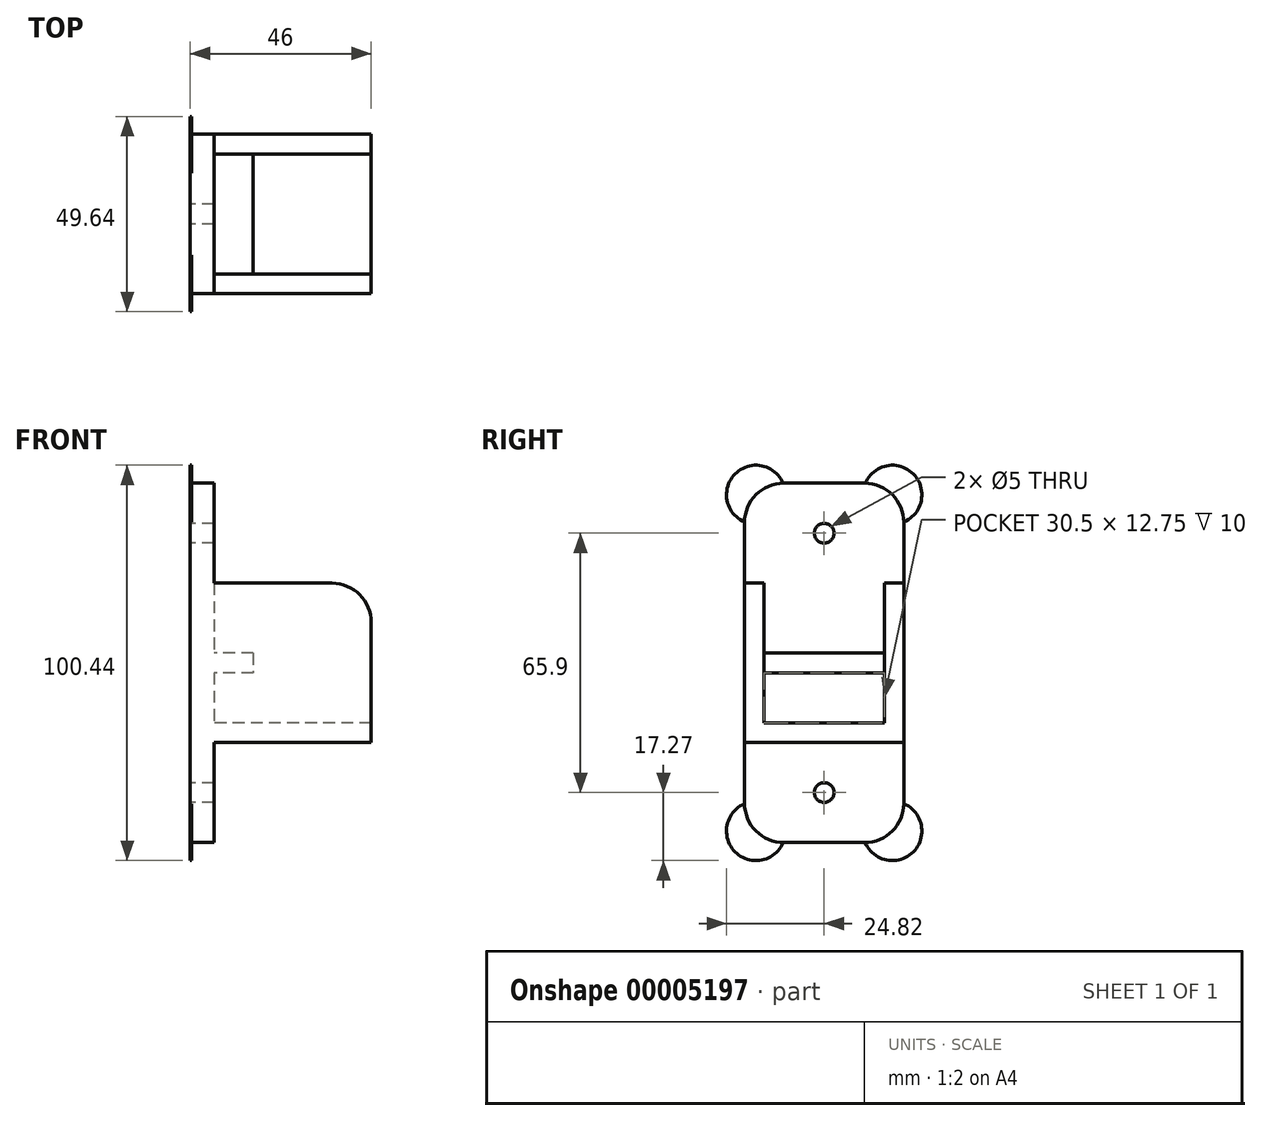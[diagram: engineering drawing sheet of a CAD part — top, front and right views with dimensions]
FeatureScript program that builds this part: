
annotation { "Feature Type Name" : "Feature", "Feature Type Description" : "" }
export const myFeature = defineFeature(function(context is Context, id is Id, definition is map)
    precondition{}
    {
        {
            var Q0;
            Q0=qCreatedBy(makeId("Right.planeOp"),FACE);
            var sketch = newSketch(context, id + "F0", { "sketchPlane" : qUnion([Q0])});
            skLineSegment(sketch, "E0.bottom", {"start": v(15.25, 15.25) * mm, "end": v(-15.25, 15.25) * mm});
            skLineSegment(sketch, "E0.top", {"start": v(15.25, -15.25) * mm, "end": v(-15.25, -15.25) * mm});
            skLineSegment(sketch, "E0.left", {"start": v(15.25, 15.25) * mm, "end": v(15.25, -15.25) * mm});
            skLineSegment(sketch, "E0.right", {"start": v(-15.25, 15.25) * mm, "end": v(-15.25, -15.25) * mm});
            skPoint(sketch, "E0.middle", {"position": v(0, 0) * mm});
            skLineSegment(sketch, "E1.bottom", {"start": v(20.25, 20.25) * mm, "end": v(-20.25, 20.25) * mm});
            skLineSegment(sketch, "E1.top", {"start": v(20.25, -20.25) * mm, "end": v(-20.25, -20.25) * mm});
            skLineSegment(sketch, "E1.left", {"start": v(20.25, 20.25) * mm, "end": v(20.25, -20.25) * mm});
            skLineSegment(sketch, "E1.right", {"start": v(-20.25, 20.25) * mm, "end": v(-20.25, -20.25) * mm});
            skSolve(sketch);
        }
        {
            var Q0;
            Q0 = qSketchRegion(id + "F0", true);
            extrude(context, id + "F1", {"entities" : qUnion([Q0]), "depth" : 40 * mm});
        }
        {
            var Q0;
            Q0=makeQuery(id+"F1.opExtrude","CAP_FACE",FACE,{"disambiguationData":[OSD([sQuery(id+"F0.wireOp",EDGE,"E0.bottom"),sQuery(id+"F0.wireOp",EDGE,"E0.top"),sQuery(id+"F0.wireOp",EDGE,"E0.left"),sQuery(id+"F0.wireOp",EDGE,"E0.right"),sQuery(id+"F0.wireOp",EDGE,"E1.bottom"),sQuery(id+"F0.wireOp",EDGE,"E1.top"),sQuery(id+"F0.wireOp",EDGE,"E1.left"),sQuery(id+"F0.wireOp",EDGE,"E1.right")])],"isStart":false});
            var sketch = newSketch(context, id + "F2", { "sketchPlane" : qUnion([Q0])});
            skLineSegment(sketch, "E2.bottom", {"start": v(15.25, 15.25) * mm, "end": v(-15.25, 15.25) * mm});
            skLineSegment(sketch, "E2.top", {"start": v(15.25, 20.25) * mm, "end": v(-15.25, 20.25) * mm});
            skLineSegment(sketch, "E2.left", {"start": v(15.25, 15.25) * mm, "end": v(15.25, 20.25) * mm});
            skLineSegment(sketch, "E2.right", {"start": v(-15.25, 15.25) * mm, "end": v(-15.25, 20.25) * mm});
            skSolve(sketch);
        }
        {
            var Q0;
            Q0 = qSketchRegion(id + "F2", true);
            extrude(context, id + "F3", {"entities" : qUnion([Q0]), "operationType" : NewBodyOperationType.REMOVE, "endBound" : BoundingType.THROUGH_ALL, "oppositeDirection" : true, "depth" : 25 * mm});
        }
        {
            var Q0;
            Q0=makeQuery(id+"F1.opExtrude","CAP_FACE",FACE,{"disambiguationData":[OSD([sQuery(id+"F0.wireOp",EDGE,"E0.bottom"),sQuery(id+"F0.wireOp",EDGE,"E0.top"),sQuery(id+"F0.wireOp",EDGE,"E0.left"),sQuery(id+"F0.wireOp",EDGE,"E0.right"),sQuery(id+"F0.wireOp",EDGE,"E1.bottom"),sQuery(id+"F0.wireOp",EDGE,"E1.top"),sQuery(id+"F0.wireOp",EDGE,"E1.left"),sQuery(id+"F0.wireOp",EDGE,"E1.right")])],"isStart":true});
            var sketch = newSketch(context, id + "F4", { "sketchPlane" : qUnion([Q0])});
            skLineSegment(sketch, "E3.bottom", {"start": v(20.25, -45.65) * mm, "end": v(-20.25, -45.65) * mm});
            skLineSegment(sketch, "E3.top", {"start": v(20.25, 45.65) * mm, "end": v(-20.25, 45.65) * mm});
            skLineSegment(sketch, "E3.left", {"start": v(20.25, -45.65) * mm, "end": v(20.25, 45.65) * mm});
            skLineSegment(sketch, "E3.right", {"start": v(-20.25, -45.65) * mm, "end": v(-20.25, 45.65) * mm});
            skPoint(sketch, "E3.middle", {"position": v(0, 0) * mm});
            skSolve(sketch);
        }
        {
            var Q0;
            Q0 = qSketchRegion(id + "F4", true);
            extrude(context, id + "F5", {"entities" : qUnion([Q0]), "operationType" : NewBodyOperationType.ADD, "depth" : 6 * mm});
        }
        {
            var Q0;
            Q0=makeQuery(id+"F5.opExtrude","SWEPT_EDGE",EDGE,{"disambiguationData":[OSD([sQuery(id+"F4.wireOp",EDGE,"E3.top"),sQuery(id+"F4.wireOp",EDGE,"E3.left")])]});
            var Q1;
            Q1=makeQuery(id+"F5.opExtrude","SWEPT_EDGE",EDGE,{"disambiguationData":[OSD([sQuery(id+"F4.wireOp",EDGE,"E3.top"),sQuery(id+"F4.wireOp",EDGE,"E3.right")])]});
            var Q2;
            {var subQ1=sQuery(id+"F0.wireOp",EDGE,"E1.bottom");var subQ2=sQuery(id+"F0.wireOp",EDGE,"E0.right");Q2=makeQuery(id+"F3.boolean.opBoolean","SPLIT",EDGE,{"disambiguationData":[TD([makeQuery(id+"F1.opExtrude","SWEPT_FACE",FACE,{"disambiguationData":[OSD([subQ2])]})])],"derivedFrom":makeQuery(id+"F1.opExtrude","CAP_EDGE",EDGE,{"disambiguationData":[OSD([subQ1])],"isStart":true})});}
            var Q3;
            {var subQ1=sQuery(id+"F0.wireOp",EDGE,"E1.bottom");var subQ2=sQuery(id+"F0.wireOp",EDGE,"E0.left");Q3=makeQuery(id+"F3.boolean.opBoolean","SPLIT",EDGE,{"disambiguationData":[TD([makeQuery(id+"F1.opExtrude","SWEPT_FACE",FACE,{"disambiguationData":[OSD([subQ2])]})])],"derivedFrom":makeQuery(id+"F1.opExtrude","CAP_EDGE",EDGE,{"disambiguationData":[OSD([subQ1])],"isStart":true})});}
            var Q4;
            Q4=makeQuery(id+"F5.opExtrude","SWEPT_EDGE",EDGE,{"disambiguationData":[OSD([sQuery(id+"F4.wireOp",EDGE,"E3.bottom"),sQuery(id+"F4.wireOp",EDGE,"E3.left")])]});
            var Q5;
            Q5=makeQuery(id+"F5.opExtrude","SWEPT_EDGE",EDGE,{"disambiguationData":[OSD([sQuery(id+"F4.wireOp",EDGE,"E3.bottom"),sQuery(id+"F4.wireOp",EDGE,"E3.right")])]});
            var Q6;
            Q6=makeQuery(id+"F1.opExtrude","CAP_EDGE",EDGE,{"disambiguationData":[OSD([sQuery(id+"F0.wireOp",EDGE,"E1.top")])],"isStart":true});
            var Q7;
            {var subQ0=sQuery(id+"F0.wireOp",EDGE,"E1.bottom");var subQ1=sQuery(id+"F0.wireOp",EDGE,"E0.right");Q7=makeQuery(id+"F3.boolean.opBoolean","SPLIT",EDGE,{"disambiguationData":[TD([makeQuery(id+"F1.opExtrude","SWEPT_FACE",FACE,{"disambiguationData":[OSD([subQ1])]})])],"derivedFrom":makeQuery(id+"F1.opExtrude","CAP_EDGE",EDGE,{"disambiguationData":[OSD([subQ0])],"isStart":false})});}
            var Q8;
            {var subQ0=sQuery(id+"F0.wireOp",EDGE,"E1.bottom");var subQ1=sQuery(id+"F0.wireOp",EDGE,"E0.left");Q8=makeQuery(id+"F3.boolean.opBoolean","SPLIT",EDGE,{"disambiguationData":[TD([makeQuery(id+"F1.opExtrude","SWEPT_FACE",FACE,{"disambiguationData":[OSD([subQ1])]})])],"derivedFrom":makeQuery(id+"F1.opExtrude","CAP_EDGE",EDGE,{"disambiguationData":[OSD([subQ0])],"isStart":false})});}
            fillet(context, id + "F6", {"entities" : qUnion([Q0, Q1, Q2, Q3, Q4, Q5, Q6, Q7, Q8]), "radius" : 10 * mm, "tangentPropagation" : true, "allowEdgeOverflow" : false});
        }
        {
            var Q0;
            Q0=makeQuery(id+"F1.opExtrude","CAP_FACE",FACE,{"disambiguationData":[OSD([sQuery(id+"F0.wireOp",EDGE,"E0.bottom"),sQuery(id+"F0.wireOp",EDGE,"E0.top"),sQuery(id+"F0.wireOp",EDGE,"E0.left"),sQuery(id+"F0.wireOp",EDGE,"E0.right"),sQuery(id+"F0.wireOp",EDGE,"E1.bottom"),sQuery(id+"F0.wireOp",EDGE,"E1.top"),sQuery(id+"F0.wireOp",EDGE,"E1.left"),sQuery(id+"F0.wireOp",EDGE,"E1.right")])],"isStart":false});
            var sketch = newSketch(context, id + "F7", { "sketchPlane" : qUnion([Q0])});
            skLineSegment(sketch, "E4.bottom", {"start": v(-15.25, -20.25) * mm, "end": v(15.25, -20.25) * mm});
            skLineSegment(sketch, "E4.top", {"start": v(-15.25, -45.65) * mm, "end": v(15.25, -45.65) * mm});
            skLineSegment(sketch, "E4.left", {"start": v(-15.25, -20.25) * mm, "end": v(-15.25, -45.65) * mm});
            skLineSegment(sketch, "E4.right", {"start": v(15.25, -20.25) * mm, "end": v(15.25, -45.65) * mm});
            skLineSegment(sketch, "E5", {"start": v(-15.25, -20.25) * mm, "end": v(-15.25, -15.25) * mm, "construction": true});
            skLineSegment(sketch, "E6", {"start": v(15.25, -20.25) * mm, "end": v(15.25, -15.25) * mm, "construction": true});
            skLineSegment(sketch, "E7.0", {"start": v(-10.25, -45.65) * mm, "end": v(10.25, -45.65) * mm, "construction": true});
            skSolve(sketch);
        }
        {
            var Q0;
            Q0 = qSketchRegion(id + "F7", true);
            var Q1;
            {var subQ0=sQuery(id+"F4.wireOp",EDGE,"E3.bottom");var subQ1=sQuery(id+"F4.wireOp",EDGE,"E3.left");var subQ2=sQuery(id+"F4.wireOp",EDGE,"E3.right");Q1=makeQuery(id+"F5.boolean.opBoolean","SPLIT",FACE,{"disambiguationData":[TD([makeQuery(id+"F1.opExtrude","SWEPT_FACE",FACE,{"disambiguationData":[OSD([sQuery(id+"F0.wireOp",EDGE,"E1.top")])]})])],"derivedFrom":makeQuery(id+"F5.opExtrude","CAP_FACE",FACE,{"disambiguationData":[OSD([subQ0,sQuery(id+"F4.wireOp",EDGE,"E3.top"),subQ1,subQ2])],"isStart":true})});}
            extrude(context, id + "F8", {"entities" : qUnion([Q0]), "operationType" : NewBodyOperationType.REMOVE, "endBound" : BoundingType.UP_TO_SURFACE, "oppositeDirection" : true, "endBoundEntityFace" : qUnion([Q1]), "depth" : 25 * mm});
        }
        {
            var Q0;
            Q0=makeQuery(id+"F5.opExtrude","CAP_FACE",FACE,{"disambiguationData":[OSD([sQuery(id+"F4.wireOp",EDGE,"E3.bottom"),sQuery(id+"F4.wireOp",EDGE,"E3.top"),sQuery(id+"F4.wireOp",EDGE,"E3.left"),sQuery(id+"F4.wireOp",EDGE,"E3.right")])],"isStart":false});
            var sketch = newSketch(context, id + "F9", { "sketchPlane" : qUnion([Q0])});
            skLineSegment(sketch, "E8", {"start": v(-20.25, 0) * mm, "end": v(20.25, 0) * mm, "construction": true});
            skLineSegment(sketch, "E9", {"start": v(0, -20.25) * mm, "end": v(0, -45.65) * mm, "construction": true});
            skCircle(sketch, "E10", {"center": v(0, -32.95) * mm, "radius": 2.5 * mm});
            skCircle(sketch, "E11.MirrorC", {"center": v(0, 32.95) * mm, "radius": 2.5 * mm});
            skLineSegment(sketch, "E12.0", {"start": v(-15.25, -20.25) * mm, "end": v(15.25, -20.25) * mm, "construction": true});
            skSolve(sketch);
        }
        {
            var Q0;
            Q0 = qSketchRegion(id + "F9", true);
            extrude(context, id + "F10", {"entities" : qUnion([Q0]), "operationType" : NewBodyOperationType.REMOVE, "endBound" : BoundingType.THROUGH_ALL, "oppositeDirection" : true, "depth" : 25 * mm});
        }
        {
            var Q0;
            {var subQ0=sQuery(id+"F4.wireOp",EDGE,"E3.top");var subQ1=sQuery(id+"F4.wireOp",EDGE,"E3.left");var subQ2=sQuery(id+"F4.wireOp",EDGE,"E3.right");Q0=makeQuery(id+"F5.boolean.opBoolean","SPLIT",FACE,{"disambiguationData":[TD([makeQuery(id+"F1.opExtrude","SWEPT_FACE",FACE,{"disambiguationData":[OSD([sQuery(id+"F0.wireOp",EDGE,"E0.top")])]})])],"derivedFrom":makeQuery(id+"F5.opExtrude","CAP_FACE",FACE,{"disambiguationData":[OSD([sQuery(id+"F4.wireOp",EDGE,"E3.bottom"),subQ0,subQ1,subQ2])],"isStart":true})});}
            var sketch = newSketch(context, id + "F11", { "sketchPlane" : qUnion([Q0])});
            skLineSegment(sketch, "E13.bottom", {"start": v(15.25, 2.5) * mm, "end": v(-15.25, 2.5) * mm});
            skLineSegment(sketch, "E13.top", {"start": v(15.25, -2.5) * mm, "end": v(-15.25, -2.5) * mm});
            skLineSegment(sketch, "E13.left", {"start": v(15.25, 2.5) * mm, "end": v(15.25, -2.5) * mm});
            skLineSegment(sketch, "E13.right", {"start": v(-15.25, 2.5) * mm, "end": v(-15.25, -2.5) * mm});
            skPoint(sketch, "E13.middle", {"position": v(0, 0) * mm});
            skSolve(sketch);
        }
        {
            var Q0;
            Q0 = qSketchRegion(id + "F11", true);
            extrude(context, id + "F12", {"entities" : qUnion([Q0]), "operationType" : NewBodyOperationType.ADD, "depth" : 10 * mm});
        }
        {
            var Q0;
            Q0=makeQuery(id+"F5.opExtrude","CAP_FACE",FACE,{"disambiguationData":[OSD([sQuery(id+"F4.wireOp",EDGE,"E3.bottom"),sQuery(id+"F4.wireOp",EDGE,"E3.top"),sQuery(id+"F4.wireOp",EDGE,"E3.left"),sQuery(id+"F4.wireOp",EDGE,"E3.right")])],"isStart":false});
            var sketch = newSketch(context, id + "F13", { "sketchPlane" : qUnion([Q0])});
            skCircle(sketch, "E14", {"center": v(17.32, -42.72) * mm, "radius": 7.5 * mm});
            skCircle(sketch, "E15", {"center": v(-17.32, -42.72) * mm, "radius": 7.5 * mm});
            skCircle(sketch, "E16", {"center": v(17.32, 42.72) * mm, "radius": 7.5 * mm});
            skCircle(sketch, "E17", {"center": v(-17.32, 42.72) * mm, "radius": 7.5 * mm});
            skSolve(sketch);
        }
        {
            var Q0;
            Q0 = qSketchRegion(id + "F13", true);
            extrude(context, id + "F14", {"entities" : qUnion([Q0]), "operationType" : NewBodyOperationType.ADD, "oppositeDirection" : true, "depth" : 0.4 * mm});
        }
    });
